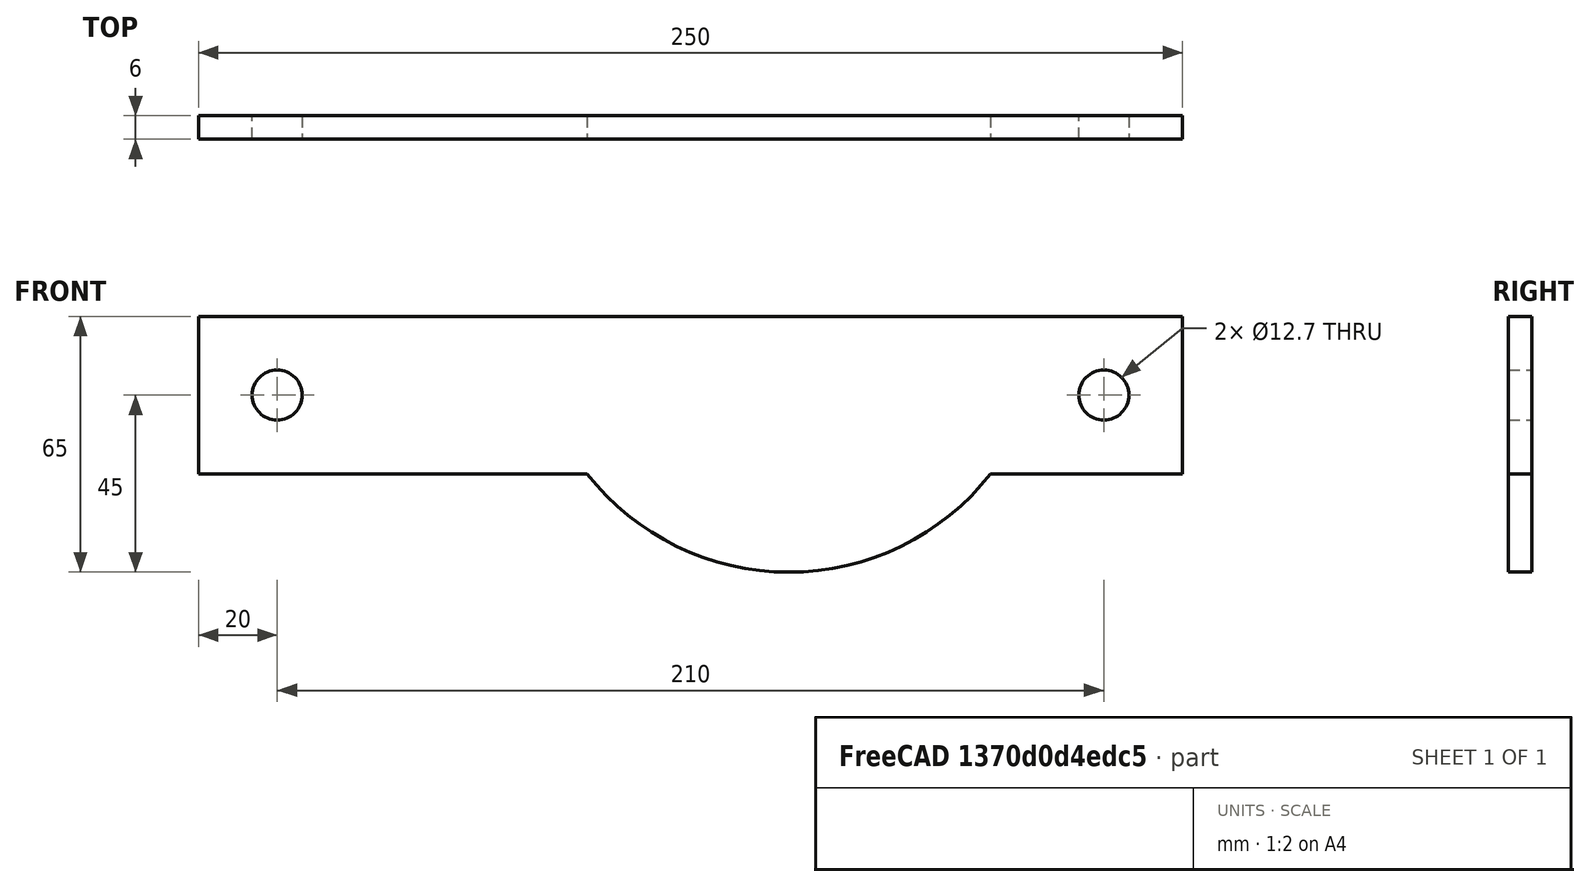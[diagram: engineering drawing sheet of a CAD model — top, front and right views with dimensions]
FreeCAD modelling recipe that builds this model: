
FCSTD DOCUMENT  (FreeCAD 0.18R4 (GitTag))
Label: palanca
License: All rights reserved
LicenseURL: http://en.wikipedia.org/wiki/All_rights_reserved
objects: Sketcher::SketchObject×1, PartDesign::Pad×1, PartDesign::Body×1
note: 4 computed .brp shape members not serialized (recipe doc carries the construction recipe); baked Part::Feature solids carry a one-line shape summary decoded from their .brp

FEATURE [Sketcher::SketchObject] Sketch
  MapMode = 5
  Placement = pos=(0,0,0) rot=(1,0,0;1.5708rad)
  Support = -> [XZ_Plane]
  sketch-geometry (8):
    g0: LineSegment StartX=0 StartY=0 StartZ=0 EndX=250 EndY=0 EndZ=0
    g1: LineSegment StartX=250 StartY=0 StartZ=0 EndX=250 EndY=-40 EndZ=0
    g2: Circle CenterX=20 CenterY=-20 CenterZ=0 NormalX=0 NormalY=0 NormalZ=1 AngleXU=0 Radius=6.35
    g3: LineSegment StartX=0 StartY=0 StartZ=0 EndX=0 EndY=-40 EndZ=0
    g4: LineSegment StartX=250 StartY=-40 StartZ=0 EndX=201.235 EndY=-40 EndZ=0
    g5: ArcOfCircle CenterX=150 CenterY=0 CenterZ=0 NormalX=0 NormalY=0 NormalZ=1 AngleXU=0 Radius=65 StartAngle=3.80447 EndAngle=5.62031
    g6: LineSegment StartX=98.7652 StartY=-40 StartZ=0 EndX=0 EndY=-40 EndZ=0
    g7: Circle CenterX=230 CenterY=-20 CenterZ=0 NormalX=0 NormalY=0 NormalZ=1 AngleXU=0 Radius=6.35
  constraints (23):
    c: Coincident(g0,g1)
    c: Horizontal(g0)
    c: Vertical(g1)
    c: DistanceX(g0,g0) = 250
    c: DistanceY(g1,g1) = 40
    c: Coincident(g0,g-1)
    c: Radius(g2) = 6.35
    c: Distance(g2,g0) = 20
    c: DistanceY(g3,g3) = 40
    c: Coincident(g0,g3)
    c: Coincident(g3,g6)
    c: Coincident(g1,g4)
    c: PointOnObject(g5,g0)
    c: Distance(g5,g3) = 150
    c: Radius(g5) = 65
    c: Tangent(g4,g6)
    c: Coincident(g5,g6)
    c: Coincident(g5,g4)
    c: Radius(g7) = 6.35
    c: Distance(g7,g1) = 20
    c: Distance(g7,g0) = 20
    c: Distance(g2,g3) = 20
    c: Vertical(g3)
FEATURE [PartDesign::Pad] Pad
  Length = 6
  Length2 = 100
  Placement = pos=(0,0,0) rot=(1,0,0;1.5708rad)
  Profile = -> Sketch
  Type = 0
FEATURE [PartDesign::Body] Body
  Group = -> [Sketch,Pad]
  Origin = -> Origin
  Tip = -> Pad
